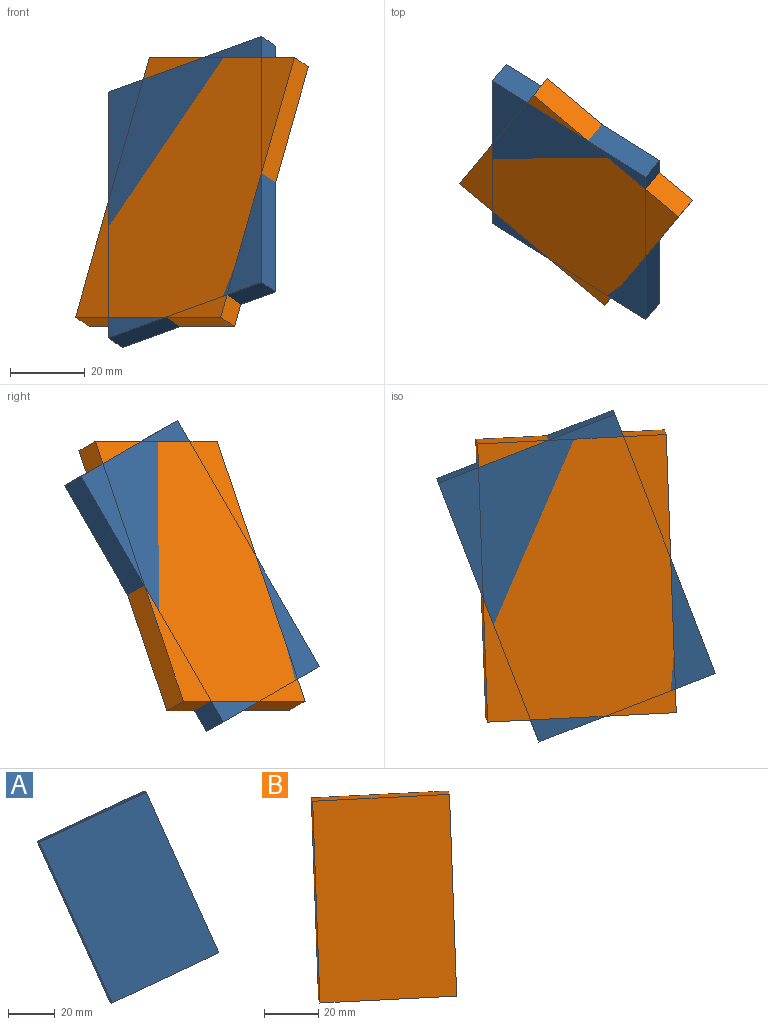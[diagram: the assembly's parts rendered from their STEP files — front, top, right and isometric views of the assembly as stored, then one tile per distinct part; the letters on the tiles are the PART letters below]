
ASSEMBLY  parts=2 mates=1
PART A: 6 faces, bbox 47.2x69x80 mm
  f0: plane 47.24x25.13mm, normal (0,0.58,0.82), area 322.6mm2, adj f1,f3,f4,f5
  f1: plane 65.46x48.4mm, normal (-0.87,0.41,-0.29), area 483.9mm2, adj f0,f2,f4,f5
  f2: plane 47.24x25.13mm, normal (0,-0.58,-0.82), area 322.6mm2, adj f1,f3,f4,f5
  f3: plane 65.46x48.4mm, normal (0.87,-0.41,0.29), area 483.9mm2, adj f0,f2,f4,f5
  f4: plane 76.82x64.52mm, normal (-0.5,-0.71,0.5), area 3871mm2, adj f0,f1,f2,f3
  f5: plane 76.82x64.52mm, normal (0.5,0.71,-0.5), area 3871mm2, adj f0,f1,f2,f3
PART B: 6 faces, bbox 62.5x60.7x72.3 mm
  f0: plane 72.26x28.06mm, normal (-0.77,0.64,0), area 483.9mm2, adj f1,f3,f4,f5
  f1: plane 42.65x37.1mm, normal (0.26,0.31,0.91), area 322.6mm2, adj f0,f2,f4,f5
  f2: plane 72.26x28.06mm, normal (0.77,-0.64,0), area 483.9mm2, adj f1,f3,f4,f5
  f3: plane 42.65x37.1mm, normal (-0.26,-0.31,-0.91), area 322.6mm2, adj f0,f2,f4,f5
  f4: plane 69.69x58.73mm, normal (-0.59,-0.7,0.4), area 3871mm2, adj f0,f1,f2,f3
  f5: plane 69.69x58.73mm, normal (0.59,0.7,-0.4), area 3871mm2, adj f0,f1,f2,f3
PLACE A rot(axis=(0.64,-0.41,-0.65),8.1deg) t=(48.51,59.35,-0.43)mm
PLACE B t=(48.51,59.35,-0.43)mm
MATE fastened A.f4 <-> B.f4  axis (-0.59,-0.7,0.4) through (44.77,54.9,2.14)mm
